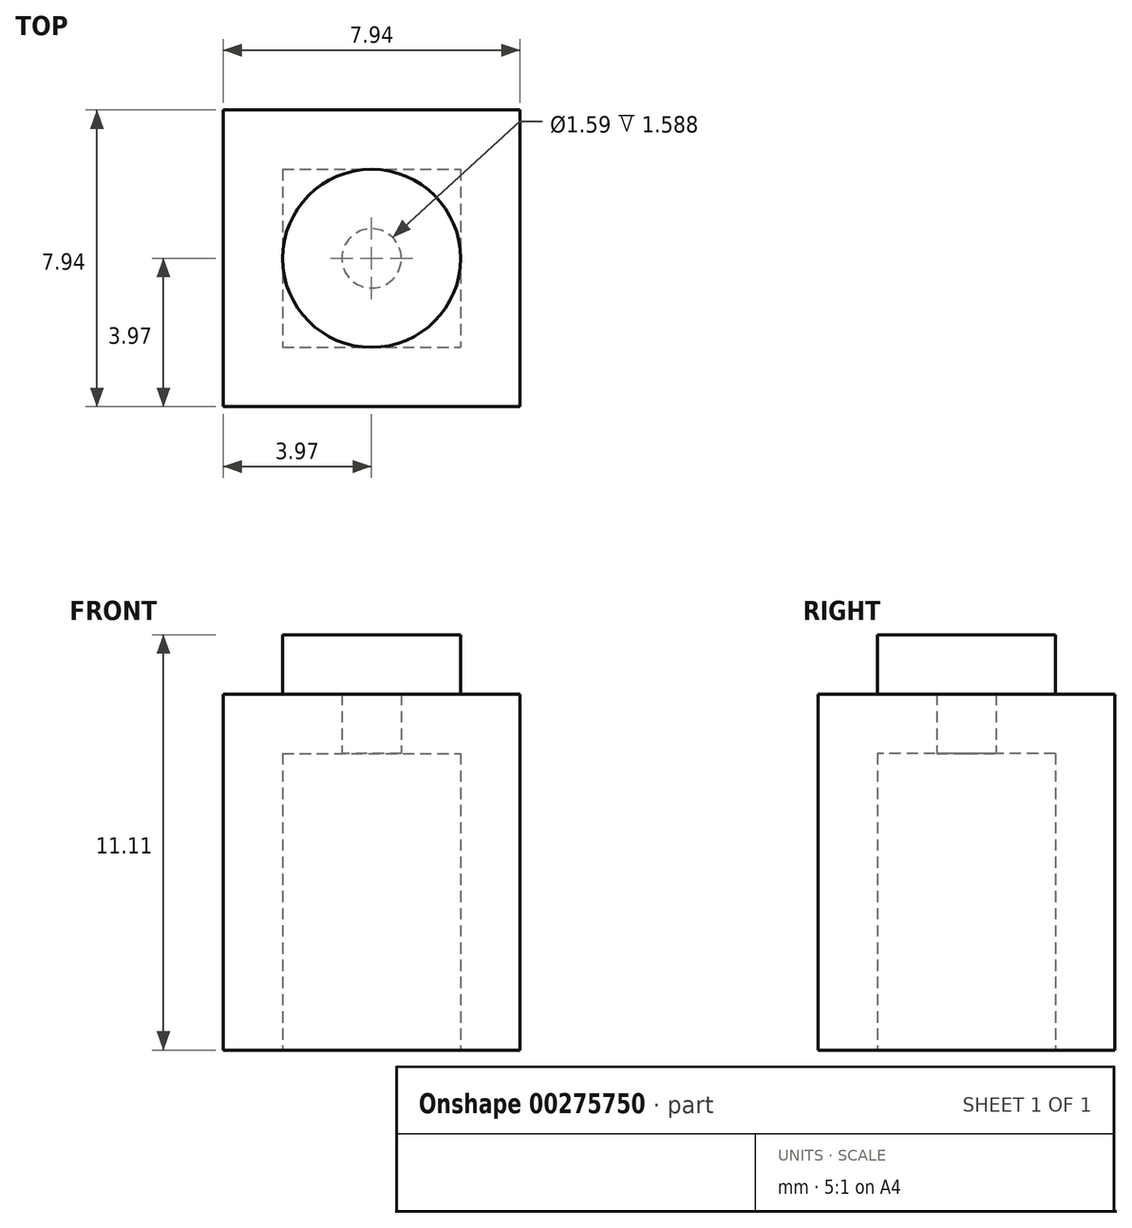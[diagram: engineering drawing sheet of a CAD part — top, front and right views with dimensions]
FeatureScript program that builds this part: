
annotation { "Feature Type Name" : "Feature", "Feature Type Description" : "" }
export const myFeature = defineFeature(function(context is Context, id is Id, definition is map)
    precondition{}
    {
        {
            var Q0;
            Q0=qCreatedBy(makeId("Top.planeOp"),FACE);
            var sketch = newSketch(context, id + "F0", { "sketchPlane" : qUnion([Q0])});
            skLineSegment(sketch, "E0.bottom", {"start": v(-3.97, 3.97) * mm, "end": v(3.97, 3.97) * mm});
            skLineSegment(sketch, "E0.top", {"start": v(-3.97, -3.97) * mm, "end": v(3.97, -3.97) * mm});
            skLineSegment(sketch, "E0.left", {"start": v(-3.97, 3.97) * mm, "end": v(-3.97, -3.97) * mm});
            skLineSegment(sketch, "E0.right", {"start": v(3.97, 3.97) * mm, "end": v(3.97, -3.97) * mm});
            skPoint(sketch, "E0.middle", {"position": v(0, 0) * mm});
            skCircle(sketch, "E1", {"center": v(0, 0) * mm, "radius": 2.38 * mm});
            skSolve(sketch);
        }
        {
            var Q0;
            Q0=qSketchRegion(id+"F0",true);
            extrude(context, id + "F1", {"entities" : qUnion([Q0]), "depth" : 9.52 * mm});
        }
        {
            var Q0;
            Q0=makeQuery(id+"F0.imprint","IMPRINT",FACE,{"disambiguationData":[TD([[makeQuery(id+"F0.imprint","IMPRINT",EDGE,{"derivedFrom":sQuery(id+"F0.wireOp",EDGE,"E1")}),1.0]])]});
            extrude(context, id + "F2", {"entities" : qUnion([Q0]), "operationType" : NewBodyOperationType.ADD, "depth" : 11.1 * mm});
        }
        {
            var Q0;
            {var subQ0=sQuery(id+"F0.wireOp",EDGE,"E1");Q0=makeQuery(id+"F2.boolean.opBoolean","MERGE",FACE,{"derivedFrom":[makeQuery(id+"F1.opExtrude","CAP_FACE",FACE,{"disambiguationData":[OSD([sQuery(id+"F0.wireOp",EDGE,"E0.bottom"),sQuery(id+"F0.wireOp",EDGE,"E0.top"),sQuery(id+"F0.wireOp",EDGE,"E0.left"),sQuery(id+"F0.wireOp",EDGE,"E0.right"),subQ0])],"isStart":true}),makeQuery(id+"F2.opExtrude","CAP_FACE",FACE,{"disambiguationData":[OSD([subQ0])],"isStart":true})]});}
            shell(context, id + "F3", {"entities" : qUnion([Q0]), "thickness" : 1.59 * mm});
        }
    });
